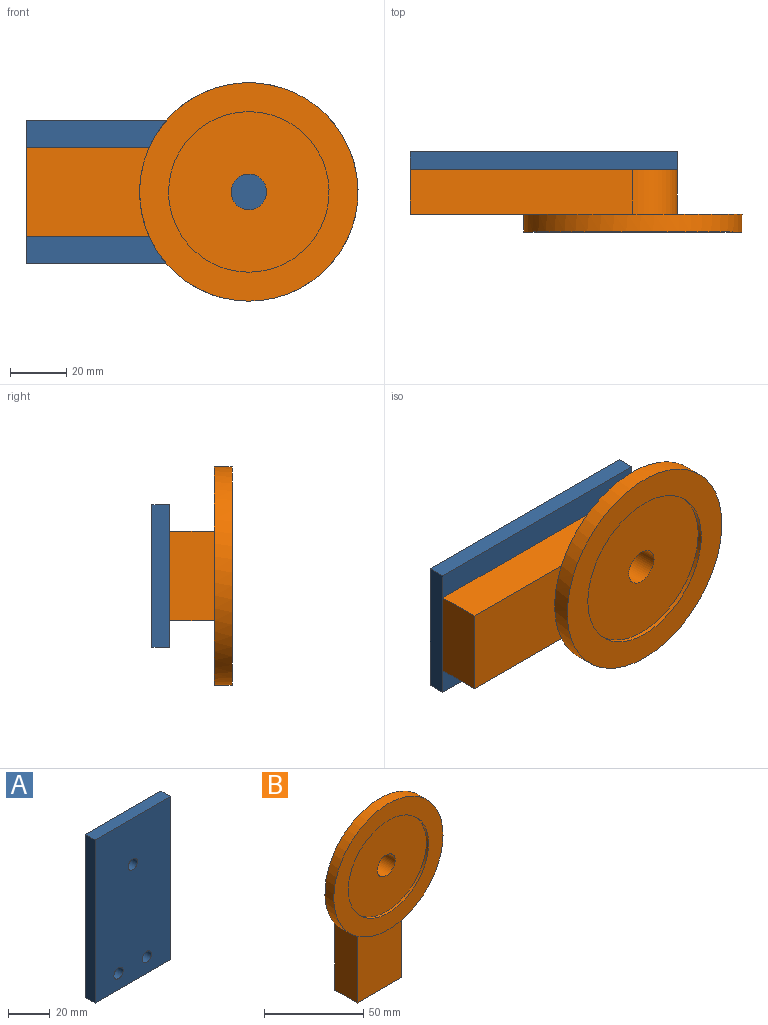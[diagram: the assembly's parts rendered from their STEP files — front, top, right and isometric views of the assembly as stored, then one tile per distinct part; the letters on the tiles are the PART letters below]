
ASSEMBLY  parts=2 mates=1
PART A: 9 faces, bbox 50.8x6.4x95.3 mm
  f0: plane 50.8x6.35mm, normal (0,0,1), area 322.6mm2, adj f1,f3,f7,f8
  f1: plane 95.25x6.35mm, normal (-1,0,0), area 604.8mm2, adj f0,f2,f7,f8
  f2: plane 50.8x6.35mm, normal (0,0,-1), area 322.6mm2, adj f1,f3,f7,f8
  f3: plane 95.25x6.35mm, normal (1,0,0), area 604.8mm2, adj f0,f2,f7,f8
  f4: cylinder r=3.17mm len=6.35mm, axis (0,1,0), area 126.7mm2, adj f7,f8
  f5: cylinder r=3.17mm len=6.35mm, axis (0,1,0), area 126.7mm2, adj f7,f8
  f6: cylinder r=3.17mm len=6.35mm, axis (0,1,0), area 126.7mm2, adj f7,f8
  f7: plane 95.25x50.8mm, normal (0,-1,0), area 4743.7mm2, adj f0,f1,f2,f3,f4,f5,f6
  f8: plane 95.25x50.8mm, normal (0,1,0), area 4743.7mm2, adj f0,f1,f2,f3,f4,f5,f6
PART B: 23 faces, bbox 77.8x22.2x118.3 mm
  f0: plane 95.25x31.75mm, normal (0,1,0), area 2083.8mm2, adj f2,f7,f8,f9,f10,f12,f13,f14
  f1: plane 57.15x57.15mm, normal (0,-1,0), area 2438.5mm2, adj f2,f5
  f2: cylinder r=6.35mm len=20.64mm, axis (0,1,0), area 823.4mm2, adj f0,f1
  f3: cylinder r=38.89mm len=77.79mm, axis (0,1,0), area 1551.8mm2, adj f4,f6,f11
  f4: plane 77.79x74.4mm, normal (0,1,0), area 3156.8mm2, adj f3,f7,f9,f10
  f5: cylinder r=28.57mm len=57.15mm, axis (0,1,0), area 285mm2, adj f1,f6
  f6: plane 77.79x77.79mm, normal (0,-1,0), area 2187.2mm2, adj f3,f5
  f7: plane 79.38x15.88mm, normal (1,0,0), area 1260.1mm2, adj f0,f4,f8,f10,f11
  f8: plane 31.75x15.88mm, normal (0,0,-1), area 504mm2, adj f0,f7,f9,f11
  f9: plane 79.38x15.88mm, normal (-1,0,0), area 1260.1mm2, adj f0,f4,f8,f10,f11
  f10: cylinder r=15.88mm len=31.75mm, axis (0,-1,0), area 791.7mm2, adj f0,f4,f7,f9
  f11: plane 43.87x31.75mm, normal (0,-1,0), area 1320.5mm2, adj f3,f7,f8,f9
  f12: plane 38.1x12.7mm, normal (-1,0.09,0), area 485.7mm2, adj f0,f13,f15,f16
  f13: cone r=6.35mm half-angle=5deg, axis (0,1,0), area 232.1mm2, adj f0,f12,f14,f16
  f14: plane 38.1x12.7mm, normal (1,0.09,0), area 485.7mm2, adj f0,f13,f15,f16
  f15: cone r=6.35mm half-angle=5deg, axis (0,1,0), area 232.1mm2, adj f0,f12,f14,f16
  f16: plane 48.58x10.48mm, normal (0,1,0), area 485.4mm2, adj f12,f13,f14,f15
  f17: cylinder r=3.17mm len=12.7mm, axis (0,1,0), area 253.4mm2, adj f0,f18
  f18: plane 6.35x6.35mm, normal (0,1,0), area 31.7mm2, adj f17
  f19: cylinder r=3.17mm len=12.7mm, axis (0,1,0), area 253.4mm2, adj f0,f20
  f20: plane 6.35x6.35mm, normal (0,1,0), area 31.7mm2, adj f19
  f21: cylinder r=3.17mm len=12.7mm, axis (0,1,0), area 253.4mm2, adj f0,f22
  f22: plane 6.35x6.35mm, normal (0,1,0), area 31.7mm2, adj f21
PLACE A rot(axis=(0,1,0),90deg) t=(-79.38,6.35,25.4)mm
PLACE B rot(axis=(0,1,0),90deg) t=(0,-15.88,0)mm
MATE fastened A.f4 <-> B.f17  axis (0,-1,0) through (-11.11,0,0)mm
